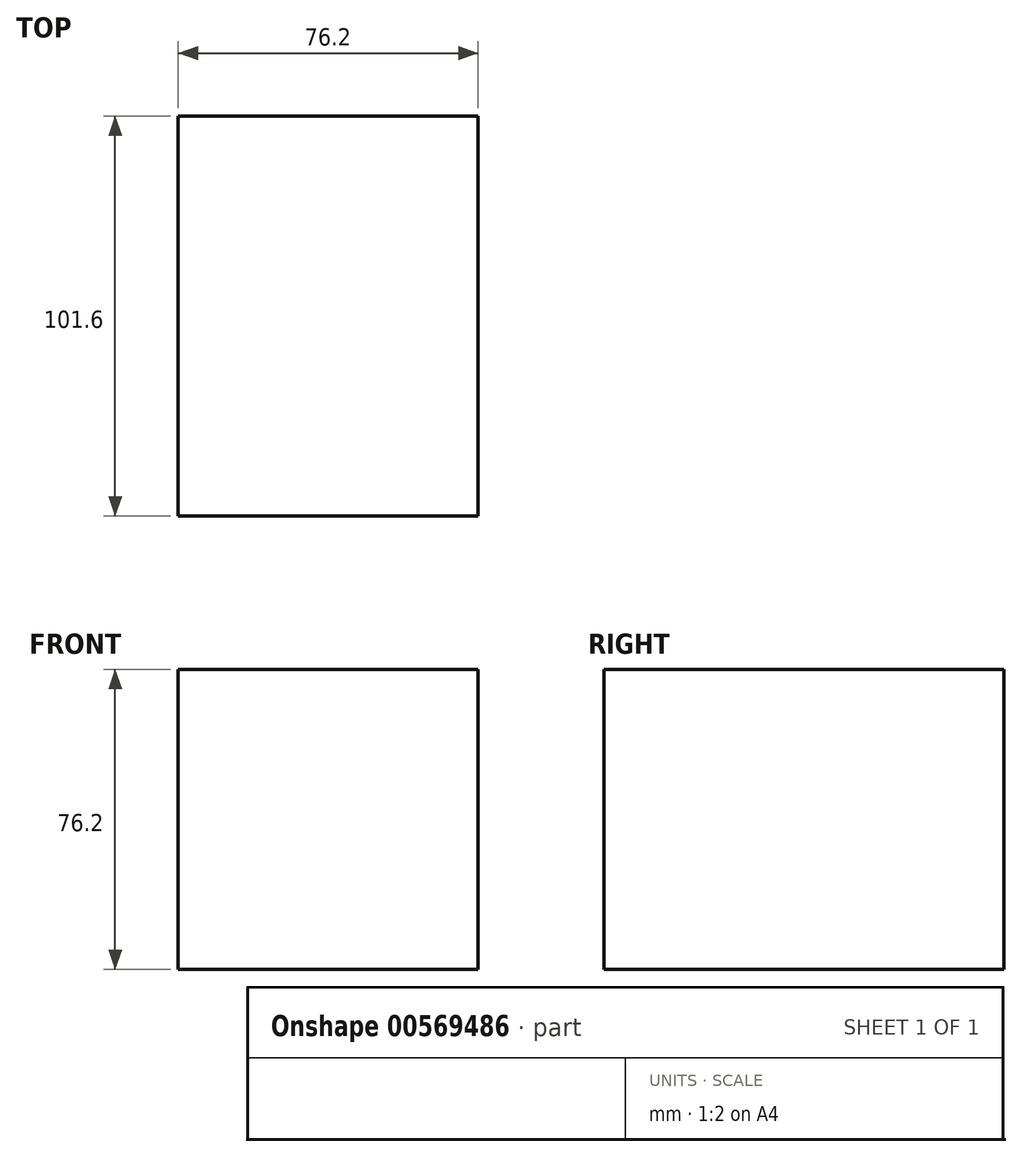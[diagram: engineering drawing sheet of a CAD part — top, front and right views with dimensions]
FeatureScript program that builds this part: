
annotation { "Feature Type Name" : "Feature", "Feature Type Description" : "" }
export const myFeature = defineFeature(function(context is Context, id is Id, definition is map)
    precondition{}
    {
        {
            var Q0;
            Q0=qCreatedBy(makeId("Front.planeOp"),FACE);
            var sketch = newSketch(context, id + "F0", { "sketchPlane" : qUnion([Q0])});
            skLineSegment(sketch, "E0.bottom", {"start": v(-45.91, 98.4) * mm, "end": v(30.29, 98.4) * mm});
            skLineSegment(sketch, "E0.top", {"start": v(-45.91, 22.2) * mm, "end": v(30.29, 22.2) * mm});
            skLineSegment(sketch, "E0.left", {"start": v(-45.91, 98.4) * mm, "end": v(-45.91, 22.2) * mm});
            skLineSegment(sketch, "E0.right", {"start": v(30.29, 98.4) * mm, "end": v(30.29, 22.2) * mm});
            skSolve(sketch);
        }
        {
            var Q0;
            Q0=makeQuery(id+"F0.imprint","IMPRINT",FACE,{"disambiguationData":[TD([[makeQuery(id+"F0.imprint","IMPRINT",EDGE,{"derivedFrom":sQuery(id+"F0.wireOp",EDGE,"E0.bottom")}),-1.0]])]});
            extrude(context, id + "F1", {"entities" : qUnion([Q0]), "depth" : 76.2 * mm, "offsetDistance" : 25.4 * mm});
        }
        {
            var Q0;
            Q0=makeQuery(id+"F1.opExtrude","CAP_FACE",FACE,{"disambiguationData":[OSD([sQuery(id+"F0.wireOp",EDGE,"E0.bottom"),sQuery(id+"F0.wireOp",EDGE,"E0.top"),sQuery(id+"F0.wireOp",EDGE,"E0.left"),sQuery(id+"F0.wireOp",EDGE,"E0.right")])],"isStart":false});
            var sketch = newSketch(context, id + "F2", { "sketchPlane" : qUnion([Q0])});
            skLineSegment(sketch, "E1.bottom", {"start": v(-29.04, 78) * mm, "end": v(-3.64, 78) * mm});
            skLineSegment(sketch, "E1.top", {"start": v(-29.04, 52.6) * mm, "end": v(-3.64, 52.6) * mm});
            skLineSegment(sketch, "E1.left", {"start": v(-29.04, 78) * mm, "end": v(-29.04, 52.6) * mm});
            skLineSegment(sketch, "E1.right", {"start": v(-3.64, 78) * mm, "end": v(-3.64, 52.6) * mm});
            skSolve(sketch);
        }
        {
            var Q0;
            Q0 = qSketchRegion(id + "F2", true);
            var Q1;
            Q1=makeQuery(id+"F2.imprint","IMPRINT",FACE,{"disambiguationData":[TD([[makeQuery(id+"F2.imprint","IMPRINT",EDGE,{"derivedFrom":sQuery(id+"F2.wireOp",EDGE,"E1.bottom")}),1.0]])]});
            extrude(context, id + "F3", {"entities" : qUnion([Q0, Q1]), "operationType" : NewBodyOperationType.ADD, "depth" : 12.7 * mm, "offsetDistance" : 25.4 * mm});
        }
        {
            var Q0;
            Q0 = qSketchRegion(id + "F2", true);
            var Q1;
            Q1=makeQuery(id+"F3.opExtrude","CAP_FACE",FACE,{"disambiguationData":[OSD([sQuery(id+"F0.wireOp",EDGE,"E0.bottom"),sQuery(id+"F0.wireOp",EDGE,"E0.top"),sQuery(id+"F0.wireOp",EDGE,"E0.left"),sQuery(id+"F0.wireOp",EDGE,"E0.right")])],"isStart":false});
            extrude(context, id + "F4", {"entities" : qUnion([Q0, Q1]), "operationType" : NewBodyOperationType.ADD, "depth" : 12.7 * mm, "offsetDistance" : 25.4 * mm});
        }
    });
